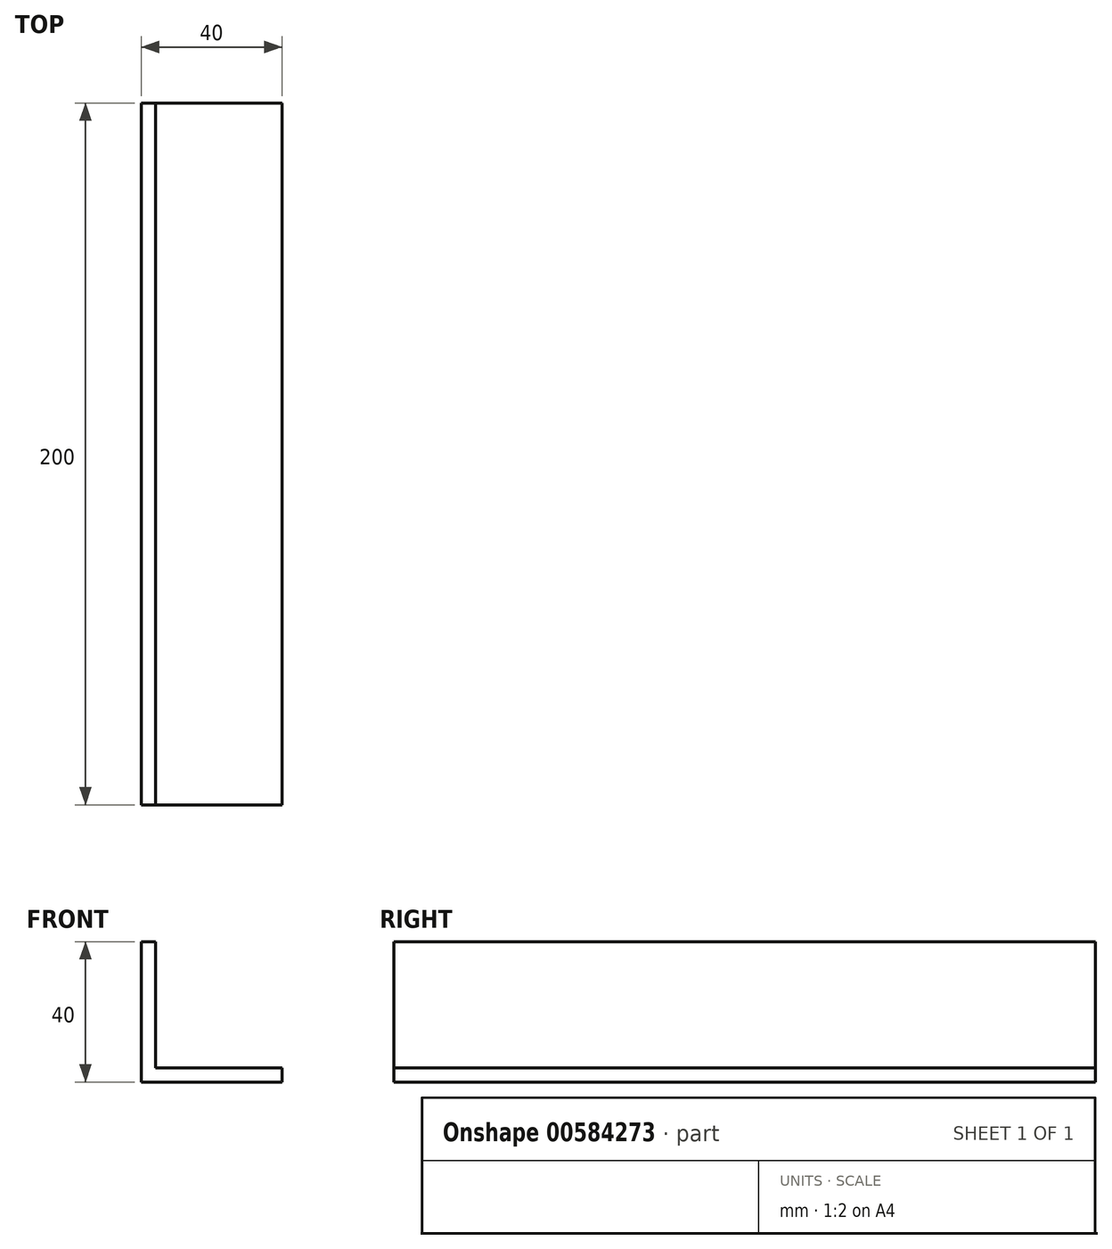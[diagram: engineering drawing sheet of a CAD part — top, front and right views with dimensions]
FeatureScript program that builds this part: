
annotation { "Feature Type Name" : "Feature", "Feature Type Description" : "" }
export const myFeature = defineFeature(function(context is Context, id is Id, definition is map)
    precondition{}
    {
        {
            var Q0;
            Q0=qCreatedBy(makeId("Front.planeOp"),FACE);
            var sketch = newSketch(context, id + "F0", { "sketchPlane" : qUnion([Q0])});
            skLineSegment(sketch, "E0", {"start": v(0, 0) * mm, "end": v(0, -40) * mm});
            skLineSegment(sketch, "E1", {"start": v(0, -40) * mm, "end": v(40, -40) * mm});
            skLineSegment(sketch, "E2", {"start": v(40, -40) * mm, "end": v(40, -36) * mm});
            skLineSegment(sketch, "E3", {"start": v(40, -36) * mm, "end": v(4, -36) * mm});
            skLineSegment(sketch, "E4", {"start": v(4, -36) * mm, "end": v(4, 0) * mm});
            skLineSegment(sketch, "E5", {"start": v(4, 0) * mm, "end": v(0, 0) * mm});
            skSolve(sketch);
        }
        {
            var Q0;
            Q0=makeQuery(id+"F0.imprint","IMPRINT",FACE,{"disambiguationData":[TD([[makeQuery(id+"F0.imprint","IMPRINT",EDGE,{"derivedFrom":sQuery(id+"F0.wireOp",EDGE,"E0")}),1.0]])]});
            extrude(context, id + "F1", {"entities" : qUnion([Q0]), "depth" : 200 * mm, "offsetDistance" : 25 * mm});
        }
    });
